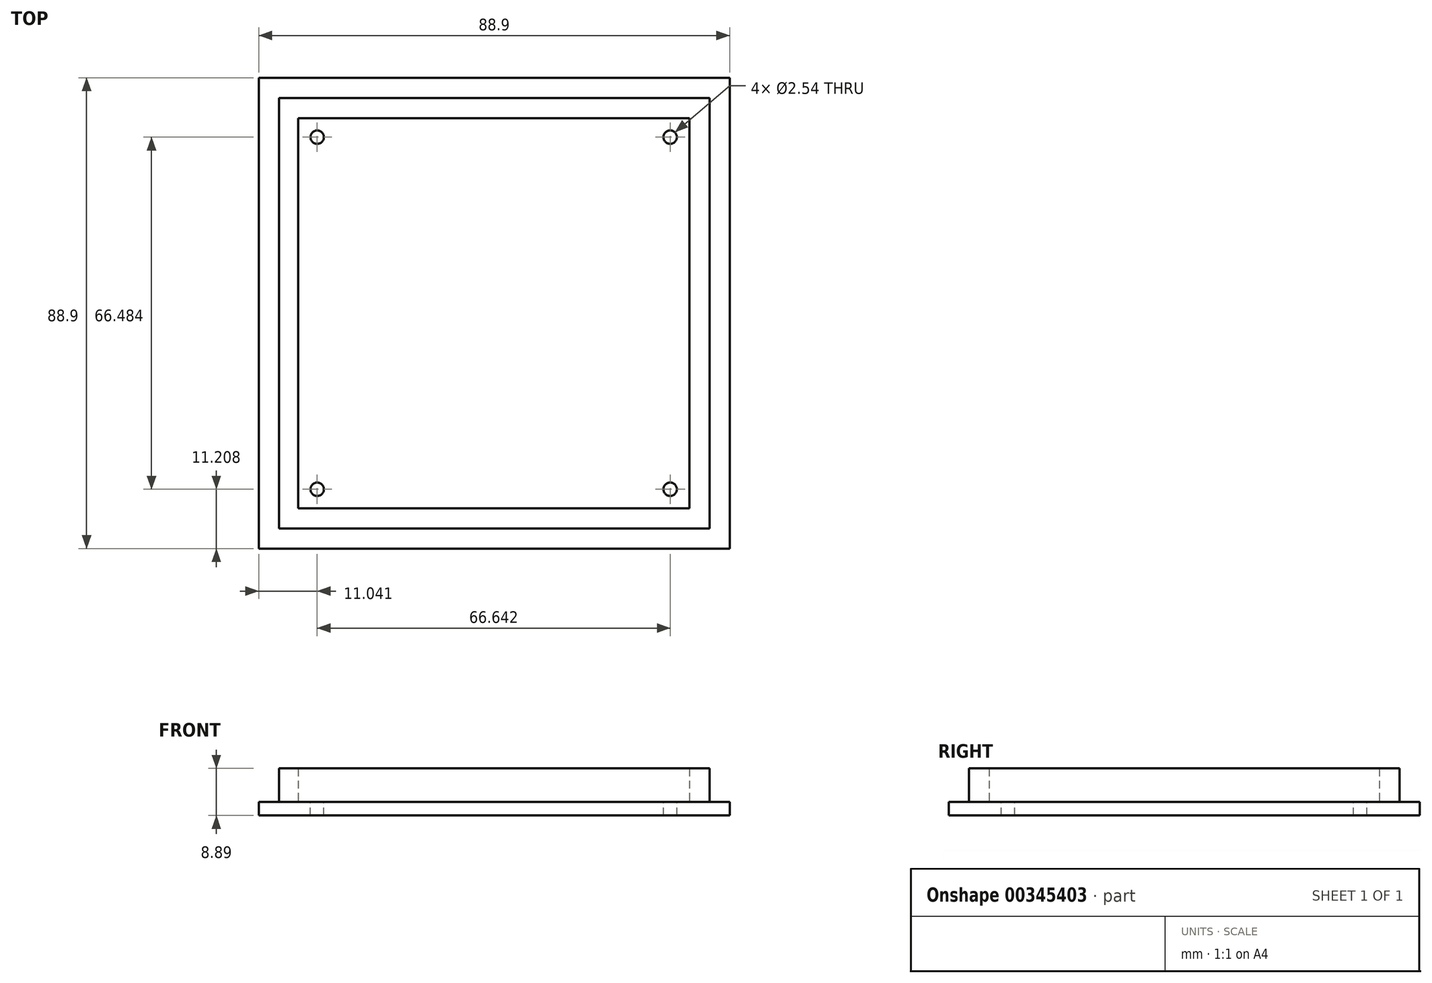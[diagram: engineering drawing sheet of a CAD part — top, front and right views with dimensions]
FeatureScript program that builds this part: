
annotation { "Feature Type Name" : "Feature", "Feature Type Description" : "" }
export const myFeature = defineFeature(function(context is Context, id is Id, definition is map)
    precondition{}
    {
        {
            var Q0;
            Q0=qCreatedBy(makeId("Top.planeOp"),FACE);
            var sketch = newSketch(context, id + "F0", { "sketchPlane" : qUnion([Q0])});
            skLineSegment(sketch, "E0.bottom", {"start": v(0, 0) * mm, "end": v(88.9, 0) * mm});
            skLineSegment(sketch, "E0.top", {"start": v(0, 88.9) * mm, "end": v(88.9, 88.9) * mm});
            skLineSegment(sketch, "E0.left", {"start": v(0, 0) * mm, "end": v(0, 88.9) * mm});
            skLineSegment(sketch, "E0.right", {"start": v(88.9, 0) * mm, "end": v(88.9, 88.9) * mm});
            skSolve(sketch);
        }
        {
            var Q0;
            Q0 = qSketchRegion(id + "F0", true);
            extrude(context, id + "F1", {"entities" : qUnion([Q0]), "depth" : 2.54 * mm});
        }
        {
            var Q0;
            Q0=makeQuery(id+"F1.opExtrude","CAP_FACE",FACE,{"disambiguationData":[OSD([sQuery(id+"F0.wireOp",EDGE,"E0.bottom"),sQuery(id+"F0.wireOp",EDGE,"E0.top"),sQuery(id+"F0.wireOp",EDGE,"E0.left"),sQuery(id+"F0.wireOp",EDGE,"E0.right")])],"isStart":false});
            var sketch = newSketch(context, id + "F2", { "sketchPlane" : qUnion([Q0])});
            skLineSegment(sketch, "E1.bottom", {"start": v(3.8, 85.1) * mm, "end": v(85.1, 85.1) * mm});
            skLineSegment(sketch, "E1.top", {"start": v(3.8, 3.8) * mm, "end": v(85.1, 3.81) * mm});
            skLineSegment(sketch, "E1.left", {"start": v(3.8, 85.1) * mm, "end": v(3.8, 3.81) * mm});
            skLineSegment(sketch, "E1.right", {"start": v(85.1, 85.1) * mm, "end": v(85.1, 3.81) * mm});
            skLineSegment(sketch, "E2.bottom", {"start": v(7.45, 81.28) * mm, "end": v(81.28, 81.28) * mm});
            skLineSegment(sketch, "E2.top", {"start": v(7.45, 7.62) * mm, "end": v(81.28, 7.62) * mm});
            skLineSegment(sketch, "E2.left", {"start": v(7.45, 81.28) * mm, "end": v(7.45, 7.62) * mm});
            skLineSegment(sketch, "E2.right", {"start": v(81.28, 81.28) * mm, "end": v(81.28, 7.62) * mm});
            skSolve(sketch);
        }
        {
            var Q0;
            Q0 = qSketchRegion(id + "F2", true);
            extrude(context, id + "F3", {"entities" : qUnion([Q0]), "operationType" : NewBodyOperationType.ADD, "depth" : 6.35 * mm});
        }
        {
            var Q0;
            Q0=makeQuery(id+"F3.boolean.opBoolean","SPLIT",FACE,{"disambiguationData":[TD([makeQuery(id+"F3.opExtrude","SWEPT_FACE",FACE,{"disambiguationData":[OSD([sQuery(id+"F2.wireOp",EDGE,"E2.bottom")])]})])],"derivedFrom":makeQuery(id+"F1.opExtrude","CAP_FACE",FACE,{"disambiguationData":[OSD([sQuery(id+"F0.wireOp",EDGE,"E0.bottom"),sQuery(id+"F0.wireOp",EDGE,"E0.top"),sQuery(id+"F0.wireOp",EDGE,"E0.left"),sQuery(id+"F0.wireOp",EDGE,"E0.right")])],"isStart":false})});
            var sketch = newSketch(context, id + "F4", { "sketchPlane" : qUnion([Q0])});
            skLineSegment(sketch, "E3", {"start": v(7.45, 81.28) * mm, "end": v(81.28, 7.62) * mm, "construction": true});
            skLineSegment(sketch, "E4", {"start": v(44.36, 81.28) * mm, "end": v(44.36, 7.62) * mm, "construction": true});
            skLineSegment(sketch, "E5", {"start": v(7.45, 44.45) * mm, "end": v(81.28, 44.45) * mm, "construction": true});
            skCircle(sketch, "E6", {"center": v(11.04, 77.7) * mm, "radius": 1.27 * mm});
            skCircle(sketch, "E7.MirrorC", {"center": v(77.68, 77.7) * mm, "radius": 1.27 * mm});
            skLineSegment(sketch, "E8.MirrorCS", {"start": v(81.28, 44.45) * mm, "end": v(7.45, 44.45) * mm, "construction": true});
            skCircle(sketch, "E9.MirrorC", {"center": v(77.68, 11.2) * mm, "radius": 1.27 * mm});
            skCircle(sketch, "E10.MirrorC", {"center": v(11.04, 11.2) * mm, "radius": 1.27 * mm});
            skSolve(sketch);
        }
        {
            var Q0;
            Q0 = qSketchRegion(id + "F4", true);
            extrude(context, id + "F5", {"entities" : qUnion([Q0]), "operationType" : NewBodyOperationType.REMOVE, "endBound" : BoundingType.THROUGH_ALL, "oppositeDirection" : true, "depth" : 25.4 * mm});
        }
    });
